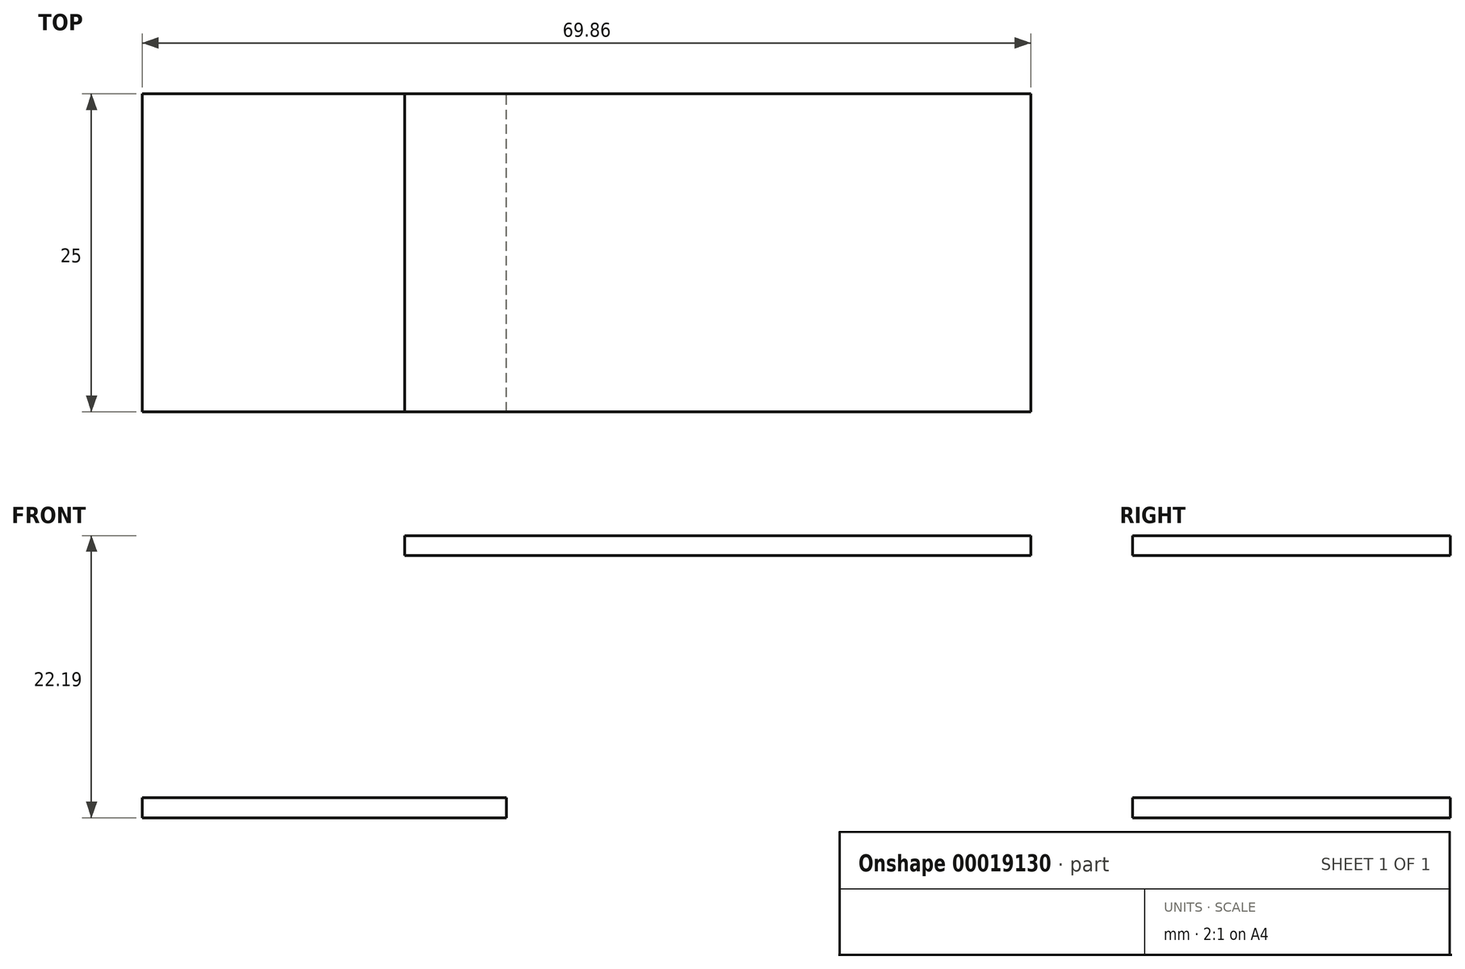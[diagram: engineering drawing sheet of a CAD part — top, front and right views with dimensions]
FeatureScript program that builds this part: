
annotation { "Feature Type Name" : "Feature", "Feature Type Description" : "" }
export const myFeature = defineFeature(function(context is Context, id is Id, definition is map)
    precondition{}
    {
        {
            var Q0;
            Q0=qCreatedBy(makeId("Front.planeOp"),FACE);
            var sketch = newSketch(context, id + "F0", { "sketchPlane" : qUnion([Q0])});
            skLineSegment(sketch, "E0", {"start": v(0, 0) * mm, "end": v(-82.48, -82.48) * mm, "construction": true});
            skLineSegment(sketch, "E1", {"start": v(82.48, -82.48) * mm, "end": v(0, 0) * mm, "construction": true});
            skLineSegment(sketch, "E2.top", {"start": v(-16.62, -22.19) * mm, "end": v(-41.24, -22.19) * mm});
            skLineSegment(sketch, "E2.left", {"start": v(-16.62, -20.62) * mm, "end": v(-16.62, -22.19) * mm});
            skLineSegment(sketch, "E2.right", {"start": v(-45.24, -20.62) * mm, "end": v(-45.24, -22.19) * mm});
            skLineSegment(sketch, "E3", {"start": v(-20.62, -1.57) * mm, "end": v(-20.62, -20.62) * mm, "construction": true});
            skLineSegment(sketch, "E4", {"start": v(-16.62, -20.62) * mm, "end": v(-20.62, -20.62) * mm});
            skLineSegment(sketch, "E5", {"start": v(-41.24, -41.24) * mm, "end": v(-41.24, -22.19) * mm, "construction": true});
            skLineSegment(sketch, "E6", {"start": v(-45.24, -22.19) * mm, "end": v(-41.24, -22.19) * mm});
            skLineSegment(sketch, "E7", {"start": v(-45.24, -20.62) * mm, "end": v(-20.62, -20.62) * mm});
            skLineSegment(sketch, "E8", {"start": v(0, 0) * mm, "end": v(-24.62, 0) * mm});
            skLineSegment(sketch, "E9", {"start": v(-24.62, 0) * mm, "end": v(-24.62, -1.57) * mm});
            skLineSegment(sketch, "E10", {"start": v(-24.62, -1.57) * mm, "end": v(-20.62, -1.57) * mm});
            skLineSegment(sketch, "E11", {"start": v(-20.62, -1.57) * mm, "end": v(0, -1.57) * mm});
            skLineSegment(sketch, "E12.top", {"start": v(-37.24, -42.81) * mm, "end": v(-61.86, -42.81) * mm});
            skLineSegment(sketch, "E12.right", {"start": v(-65.86, -41.24) * mm, "end": v(-65.86, -42.81) * mm});
            skLineSegment(sketch, "E13", {"start": v(-37.24, -41.24) * mm, "end": v(-41.24, -41.24) * mm});
            skLineSegment(sketch, "E14", {"start": v(-65.86, -41.24) * mm, "end": v(-41.24, -41.24) * mm});
            skLineSegment(sketch, "E12.left", {"start": v(-37.24, -41.24) * mm, "end": v(-37.24, -42.81) * mm});
            skLineSegment(sketch, "E15", {"start": v(-65.86, -42.81) * mm, "end": v(-61.86, -42.81) * mm});
            skLineSegment(sketch, "E16", {"start": v(-86.48, -63.43) * mm, "end": v(-82.48, -63.43) * mm});
            skLineSegment(sketch, "E17", {"start": v(-61.86, -61.86) * mm, "end": v(-61.86, -42.81) * mm, "construction": true});
            skLineSegment(sketch, "E18", {"start": v(-86.48, -61.86) * mm, "end": v(-61.86, -61.86) * mm});
            skLineSegment(sketch, "E19.top", {"start": v(-57.86, -63.43) * mm, "end": v(-82.48, -63.43) * mm});
            skLineSegment(sketch, "E20", {"start": v(-57.86, -61.86) * mm, "end": v(-61.86, -61.86) * mm});
            skLineSegment(sketch, "E19.left", {"start": v(-57.86, -61.86) * mm, "end": v(-57.86, -63.43) * mm});
            skLineSegment(sketch, "E19.right", {"start": v(-86.48, -61.86) * mm, "end": v(-86.48, -63.43) * mm});
            skLineSegment(sketch, "E21", {"start": v(-107.1, -84.05) * mm, "end": v(-103.1, -84.05) * mm});
            skLineSegment(sketch, "E22", {"start": v(-82.48, -82.48) * mm, "end": v(-82.48, -63.43) * mm, "construction": true});
            skLineSegment(sketch, "E23", {"start": v(-107.1, -82.48) * mm, "end": v(-82.48, -82.48) * mm});
            skLineSegment(sketch, "E24.top", {"start": v(-78.48, -84.05) * mm, "end": v(-103.1, -84.05) * mm});
            skLineSegment(sketch, "E25", {"start": v(-78.48, -82.48) * mm, "end": v(-82.48, -82.48) * mm});
            skLineSegment(sketch, "E24.left", {"start": v(-78.48, -82.48) * mm, "end": v(-78.48, -84.05) * mm});
            skLineSegment(sketch, "E24.right", {"start": v(-107.1, -82.48) * mm, "end": v(-107.1, -84.05) * mm});
            skLineSegment(sketch, "E26", {"start": v(0, 0) * mm, "end": v(0, -82.48) * mm, "construction": true});
            skLineSegment(sketch, "E27.MirrorCS", {"start": v(65.86, -41.24) * mm, "end": v(65.86, -42.81) * mm});
            skLineSegment(sketch, "E28.MirrorCS", {"start": v(45.24, -20.62) * mm, "end": v(45.24, -22.19) * mm});
            skLineSegment(sketch, "E29.MirrorCS", {"start": v(78.48, -82.48) * mm, "end": v(82.48, -82.48) * mm});
            skLineSegment(sketch, "E30.MirrorCS", {"start": v(78.48, -82.48) * mm, "end": v(78.48, -84.05) * mm});
            skLineSegment(sketch, "E31.MirrorCS", {"start": v(16.62, -20.62) * mm, "end": v(16.62, -22.19) * mm});
            skLineSegment(sketch, "E32.MirrorCS", {"start": v(37.24, -41.24) * mm, "end": v(41.24, -41.24) * mm});
            skLineSegment(sketch, "E33.MirrorCS", {"start": v(57.86, -61.86) * mm, "end": v(57.86, -63.43) * mm});
            skLineSegment(sketch, "E34.MirrorCS", {"start": v(57.86, -61.86) * mm, "end": v(61.86, -61.86) * mm});
            skLineSegment(sketch, "E35.MirrorCS", {"start": v(86.48, -61.86) * mm, "end": v(86.48, -63.43) * mm});
            skLineSegment(sketch, "E36.MirrorCS", {"start": v(107.1, -82.48) * mm, "end": v(107.1, -84.05) * mm});
            skLineSegment(sketch, "E37.MirrorCS", {"start": v(37.24, -41.24) * mm, "end": v(37.24, -42.81) * mm});
            skLineSegment(sketch, "E38.MirrorCS", {"start": v(65.86, -42.81) * mm, "end": v(61.86, -42.81) * mm});
            skLineSegment(sketch, "E39.MirrorCS", {"start": v(45.24, -22.19) * mm, "end": v(41.24, -22.19) * mm});
            skLineSegment(sketch, "E40.MirrorCS", {"start": v(86.48, -63.43) * mm, "end": v(82.48, -63.43) * mm});
            skLineSegment(sketch, "E41.MirrorCS", {"start": v(107.1, -84.05) * mm, "end": v(103.1, -84.05) * mm});
            skLineSegment(sketch, "E42.MirrorCS", {"start": v(16.62, -20.62) * mm, "end": v(20.62, -20.62) * mm});
            skLineSegment(sketch, "E43.MirrorCS", {"start": v(37.24, -42.81) * mm, "end": v(61.86, -42.81) * mm});
            skLineSegment(sketch, "E44.MirrorCS", {"start": v(16.62, -22.19) * mm, "end": v(41.24, -22.19) * mm});
            skLineSegment(sketch, "E45.MirrorCS", {"start": v(86.48, -61.86) * mm, "end": v(61.86, -61.86) * mm});
            skLineSegment(sketch, "E46.MirrorCS", {"start": v(57.86, -63.43) * mm, "end": v(82.48, -63.43) * mm});
            skPoint(sketch, "E47.MirrorP", {"position": v(20.62, -20.62) * mm});
            skLineSegment(sketch, "E48.MirrorCS", {"start": v(78.48, -84.05) * mm, "end": v(103.1, -84.05) * mm});
            skPoint(sketch, "E49.MirrorP", {"position": v(82.48, -82.48) * mm});
            skPoint(sketch, "E50.MirrorP", {"position": v(61.86, -61.86) * mm});
            skLineSegment(sketch, "E51.MirrorCS", {"start": v(41.24, -41.24) * mm, "end": v(41.24, -22.19) * mm});
            skPoint(sketch, "E52.MirrorP", {"position": v(41.24, -41.24) * mm});
            skLineSegment(sketch, "E53.MirrorCS", {"start": v(61.86, -61.86) * mm, "end": v(61.86, -42.81) * mm});
            skLineSegment(sketch, "E54.MirrorCS", {"start": v(45.24, -20.62) * mm, "end": v(20.62, -20.62) * mm});
            skLineSegment(sketch, "E55.MirrorCS", {"start": v(107.1, -82.48) * mm, "end": v(82.48, -82.48) * mm});
            skLineSegment(sketch, "E56.MirrorCS", {"start": v(65.86, -41.24) * mm, "end": v(41.24, -41.24) * mm});
            skLineSegment(sketch, "E57.MirrorCS", {"start": v(82.48, -82.48) * mm, "end": v(82.48, -63.43) * mm});
            skLineSegment(sketch, "E58.MirrorCS", {"start": v(20.62, -1.57) * mm, "end": v(0, -1.57) * mm});
            skLineSegment(sketch, "E59.MirrorCS", {"start": v(24.62, -1.57) * mm, "end": v(20.62, -1.57) * mm});
            skLineSegment(sketch, "E60.MirrorCS", {"start": v(0, 0) * mm, "end": v(24.62, 0) * mm});
            skLineSegment(sketch, "E61.MirrorCS", {"start": v(24.62, 0) * mm, "end": v(24.62, -1.57) * mm});
            skLineSegment(sketch, "E62", {"start": v(-82.48, -82.48) * mm, "end": v(82.48, -82.48) * mm, "construction": true});
            skPoint(sketch, "E63", {"position": v(0, -82.48) * mm});
            skLineSegment(sketch, "E64", {"start": v(20.62, -1.57) * mm, "end": v(20.62, -20.62) * mm, "construction": true});
            skPoint(sketch, "E65", {"position": v(16.62, -20.62) * mm});
            skPoint(sketch, "E66", {"position": v(45.24, -20.62) * mm});
            skPoint(sketch, "E67", {"position": v(37.24, -41.24) * mm});
            skPoint(sketch, "E68", {"position": v(65.86, -41.24) * mm});
            skPoint(sketch, "E69", {"position": v(57.86, -61.86) * mm});
            skPoint(sketch, "E70", {"position": v(86.48, -61.86) * mm});
            skPoint(sketch, "E71", {"position": v(78.48, -82.48) * mm});
            skPoint(sketch, "E72", {"position": v(107.1, -82.48) * mm});
            skPoint(sketch, "E73", {"position": v(24.62, 0) * mm});
            skPoint(sketch, "E74", {"position": v(0, 0) * mm});
            skLineSegment(sketch, "E75", {"start": v(16.62, -20.62) * mm, "end": v(14.62, -20.62) * mm, "construction": true});
            skPoint(sketch, "E76", {"position": v(14.62, -20.62) * mm});
            skLineSegment(sketch, "E77", {"start": v(37.24, -41.24) * mm, "end": v(35.24, -41.24) * mm, "construction": true});
            skLineSegment(sketch, "E78", {"start": v(57.86, -61.86) * mm, "end": v(55.86, -61.86) * mm, "construction": true});
            skLineSegment(sketch, "E79", {"start": v(78.48, -82.48) * mm, "end": v(76.48, -82.48) * mm, "construction": true});
            skPoint(sketch, "E80", {"position": v(35.24, -41.24) * mm});
            skPoint(sketch, "E81", {"position": v(55.86, -61.86) * mm});
            skPoint(sketch, "E82", {"position": v(76.48, -82.48) * mm});
            skSolve(sketch);
        }
        {
            var Q0;
            Q0=makeQuery(id+"F0.imprint","IMPRINT",FACE,{"disambiguationData":[TD([[makeQuery(id+"F0.imprint","IMPRINT",EDGE,{"derivedFrom":sQuery(id+"F0.wireOp",EDGE,"E2.top")}),-1.0]])]});
            var Q1;
            Q1=makeQuery(id+"F0.imprint","IMPRINT",FACE,{"disambiguationData":[TD([[makeQuery(id+"F0.imprint","IMPRINT",EDGE,{"derivedFrom":sQuery(id+"F0.wireOp",EDGE,"E8")}),1.0]])]});
            extrude(context, id + "F1", {"entities" : qUnion([Q0, Q1]), "depth" : 25 * mm, "symmetric" : true});
        }
    });
